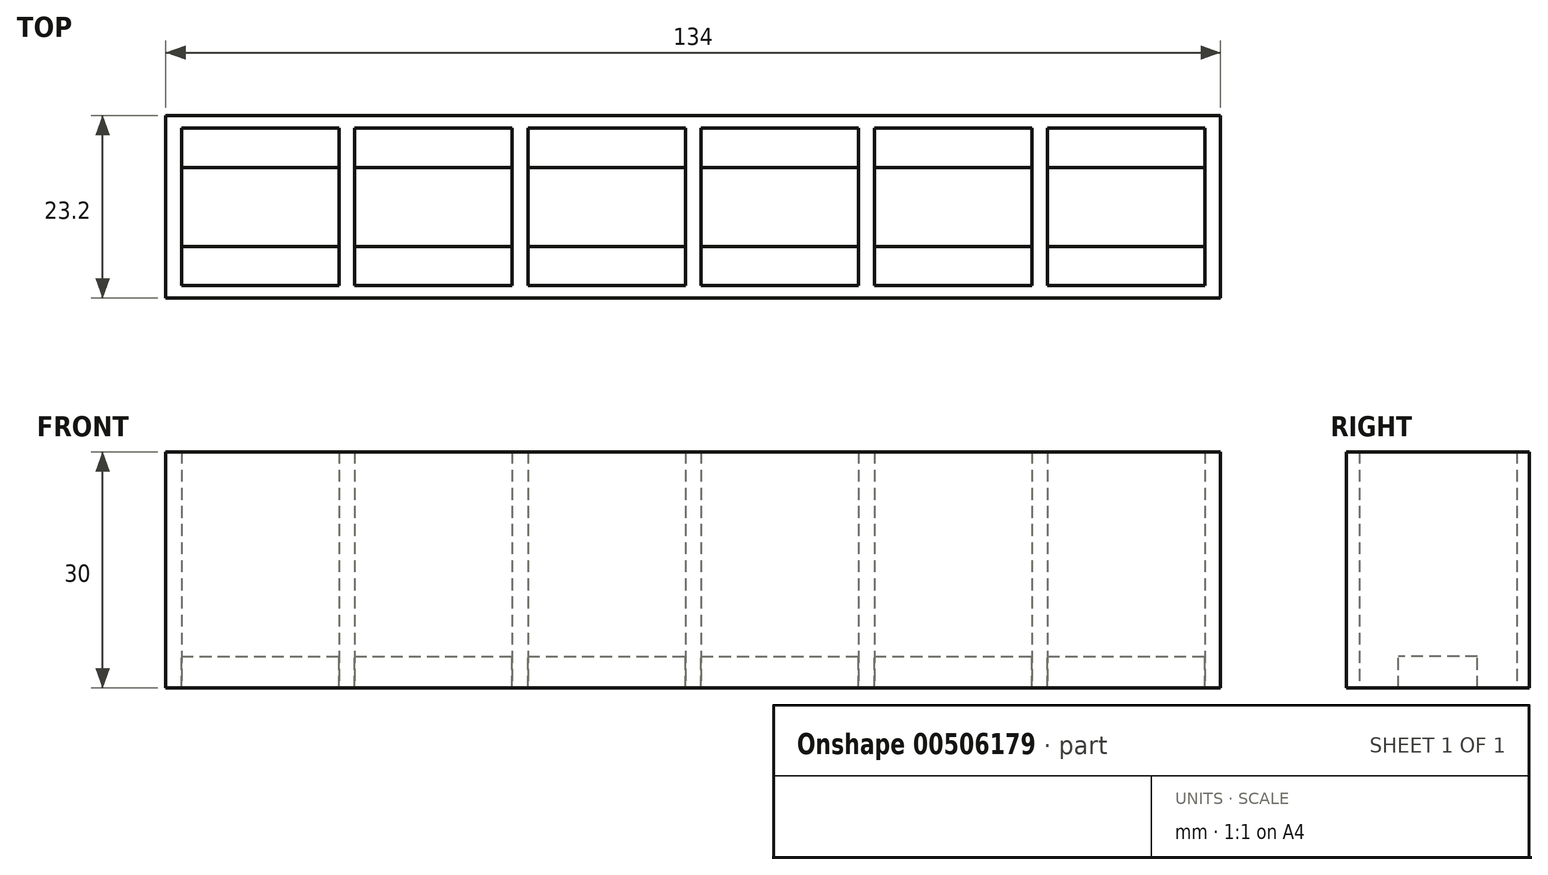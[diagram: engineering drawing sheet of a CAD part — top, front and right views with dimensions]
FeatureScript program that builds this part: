
annotation { "Feature Type Name" : "Feature", "Feature Type Description" : "" }
export const myFeature = defineFeature(function(context is Context, id is Id, definition is map)
    precondition{}
    {
        {
            var Q0;
            Q0=qCreatedBy(makeId("Top.planeOp"),FACE);
            var sketch = newSketch(context, id + "F0", { "sketchPlane" : qUnion([Q0])});
            skLineSegment(sketch, "E0.bottom", {"start": v(-66, 23.2) * mm, "end": v(68, 23.2) * mm});
            skLineSegment(sketch, "E0.top", {"start": v(-66, 0) * mm, "end": v(68, 0) * mm});
            skLineSegment(sketch, "E0.left", {"start": v(-66, 23.2) * mm, "end": v(-66, 0) * mm});
            skLineSegment(sketch, "E0.right", {"start": v(68, 23.2) * mm, "end": v(68, 0) * mm});
            skLineSegment(sketch, "E1.bottom", {"start": v(-64, 21.6) * mm, "end": v(-44, 21.6) * mm});
            skLineSegment(sketch, "E1.top", {"start": v(-64, 1.6) * mm, "end": v(-44, 1.6) * mm});
            skLineSegment(sketch, "E1.left", {"start": v(-64, 21.6) * mm, "end": v(-64, 1.6) * mm});
            skLineSegment(sketch, "E1.right", {"start": v(-44, 21.6) * mm, "end": v(-44, 1.6) * mm});
            skLineSegment(sketch, "E2.1.0.0", {"start": v(-22, 21.6) * mm, "end": v(-22, 1.6) * mm});
            skLineSegment(sketch, "E2.1.0.1", {"start": v(-42, 21.6) * mm, "end": v(-42, 1.6) * mm});
            skLineSegment(sketch, "E2.1.0.2", {"start": v(-42, 1.6) * mm, "end": v(-22, 1.6) * mm});
            skLineSegment(sketch, "E2.1.0.3", {"start": v(-42, 21.6) * mm, "end": v(-22, 21.6) * mm});
            skLineSegment(sketch, "E2.2.0.0", {"start": v(0, 21.6) * mm, "end": v(0, 1.6) * mm});
            skLineSegment(sketch, "E2.2.0.1", {"start": v(-20, 21.6) * mm, "end": v(-20, 1.6) * mm});
            skLineSegment(sketch, "E2.2.0.2", {"start": v(-20, 1.6) * mm, "end": v(0, 1.6) * mm});
            skLineSegment(sketch, "E2.2.0.3", {"start": v(-20, 21.6) * mm, "end": v(0, 21.6) * mm});
            skLineSegment(sketch, "E2.3.0.0", {"start": v(22, 21.6) * mm, "end": v(22, 1.6) * mm});
            skLineSegment(sketch, "E2.3.0.1", {"start": v(2, 21.6) * mm, "end": v(2, 1.6) * mm});
            skLineSegment(sketch, "E2.3.0.2", {"start": v(2, 1.6) * mm, "end": v(22, 1.6) * mm});
            skLineSegment(sketch, "E2.3.0.3", {"start": v(2, 21.6) * mm, "end": v(22, 21.6) * mm});
            skLineSegment(sketch, "E2.4.0.0", {"start": v(44, 21.6) * mm, "end": v(44, 1.6) * mm});
            skLineSegment(sketch, "E2.4.0.1", {"start": v(24, 21.6) * mm, "end": v(24, 1.6) * mm});
            skLineSegment(sketch, "E2.4.0.2", {"start": v(24, 1.6) * mm, "end": v(44, 1.6) * mm});
            skLineSegment(sketch, "E2.4.0.3", {"start": v(24, 21.6) * mm, "end": v(44, 21.6) * mm});
            skLineSegment(sketch, "E2.5.0.0", {"start": v(66, 21.6) * mm, "end": v(66, 1.6) * mm});
            skLineSegment(sketch, "E2.5.0.1", {"start": v(46, 21.6) * mm, "end": v(46, 1.6) * mm});
            skLineSegment(sketch, "E2.5.0.2", {"start": v(46, 1.6) * mm, "end": v(66, 1.6) * mm});
            skLineSegment(sketch, "E2.5.0.3", {"start": v(46, 21.6) * mm, "end": v(66, 21.6) * mm});
            skLineSegment(sketch, "E2.direction1", {"start": v(-64, 1.6) * mm, "end": v(-42, 1.6) * mm, "construction": true});
            skSolve(sketch);
        }
        {
            var Q0;
            Q0 = qSketchRegion(id + "F0", true);
            extrude(context, id + "F1", {"entities" : qUnion([Q0]), "depth" : 30 * mm});
        }
        {
            var Q0;
            Q0=qCreatedBy(makeId("Top.planeOp"),FACE);
            var sketch = newSketch(context, id + "F2", { "sketchPlane" : qUnion([Q0])});
            skLineSegment(sketch, "E3.bottom", {"start": v(-65, 16.6) * mm, "end": v(67, 16.6) * mm});
            skLineSegment(sketch, "E3.top", {"start": v(-65, 6.6) * mm, "end": v(67, 6.6) * mm});
            skLineSegment(sketch, "E3.left", {"start": v(-65, 16.6) * mm, "end": v(-65, 6.6) * mm});
            skLineSegment(sketch, "E3.right", {"start": v(67, 16.6) * mm, "end": v(67, 6.6) * mm});
            skSolve(sketch);
        }
        {
            var Q0;
            Q0 = qSketchRegion(id + "F2", true);
            extrude(context, id + "F3", {"entities" : qUnion([Q0]), "operationType" : NewBodyOperationType.ADD, "depth" : 4 * mm});
        }
    });
